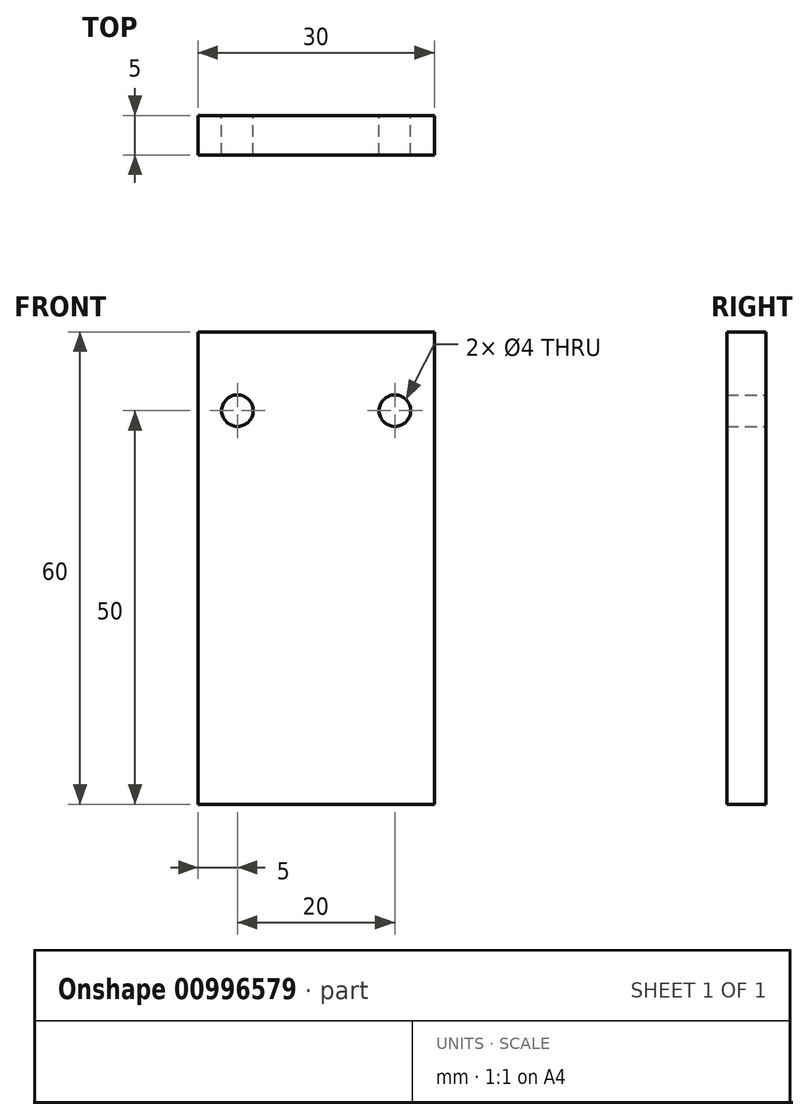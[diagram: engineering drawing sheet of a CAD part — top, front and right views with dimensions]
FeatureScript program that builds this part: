
annotation { "Feature Type Name" : "Feature", "Feature Type Description" : "" }
export const myFeature = defineFeature(function(context is Context, id is Id, definition is map)
    precondition{}
    {
        {
            var Q0;
            Q0=qCreatedBy(makeId("Front.planeOp"),FACE);
            var sketch = newSketch(context, id + "F0", { "sketchPlane" : qUnion([Q0])});
            skLineSegment(sketch, "E0.bottom", {"start": v(0, 0) * mm, "end": v(30, 0) * mm});
            skLineSegment(sketch, "E0.top", {"start": v(0, 60) * mm, "end": v(30, 60) * mm});
            skLineSegment(sketch, "E0.left", {"start": v(0, 0) * mm, "end": v(0, 60) * mm});
            skLineSegment(sketch, "E0.right", {"start": v(30, 0) * mm, "end": v(30, 60) * mm});
            skLineSegment(sketch, "E1", {"start": v(15, 60) * mm, "end": v(15, 0) * mm, "construction": true});
            skCircle(sketch, "E2", {"center": v(5, 50) * mm, "radius": 2 * mm});
            skCircle(sketch, "E3.MirrorC", {"center": v(25, 50) * mm, "radius": 2 * mm});
            skSolve(sketch);
        }
        {
            var Q0;
            Q0=makeQuery(id+"F0.imprint","IMPRINT",FACE,{"disambiguationData":[TD([[makeQuery(id+"F0.imprint","IMPRINT",EDGE,{"derivedFrom":sQuery(id+"F0.wireOp",EDGE,"E0.bottom")}),1.0]])]});
            extrude(context, id + "F1", {"entities" : qUnion([Q0]), "depth" : 5 * mm, "offsetDistance" : 25 * mm});
        }
    });
